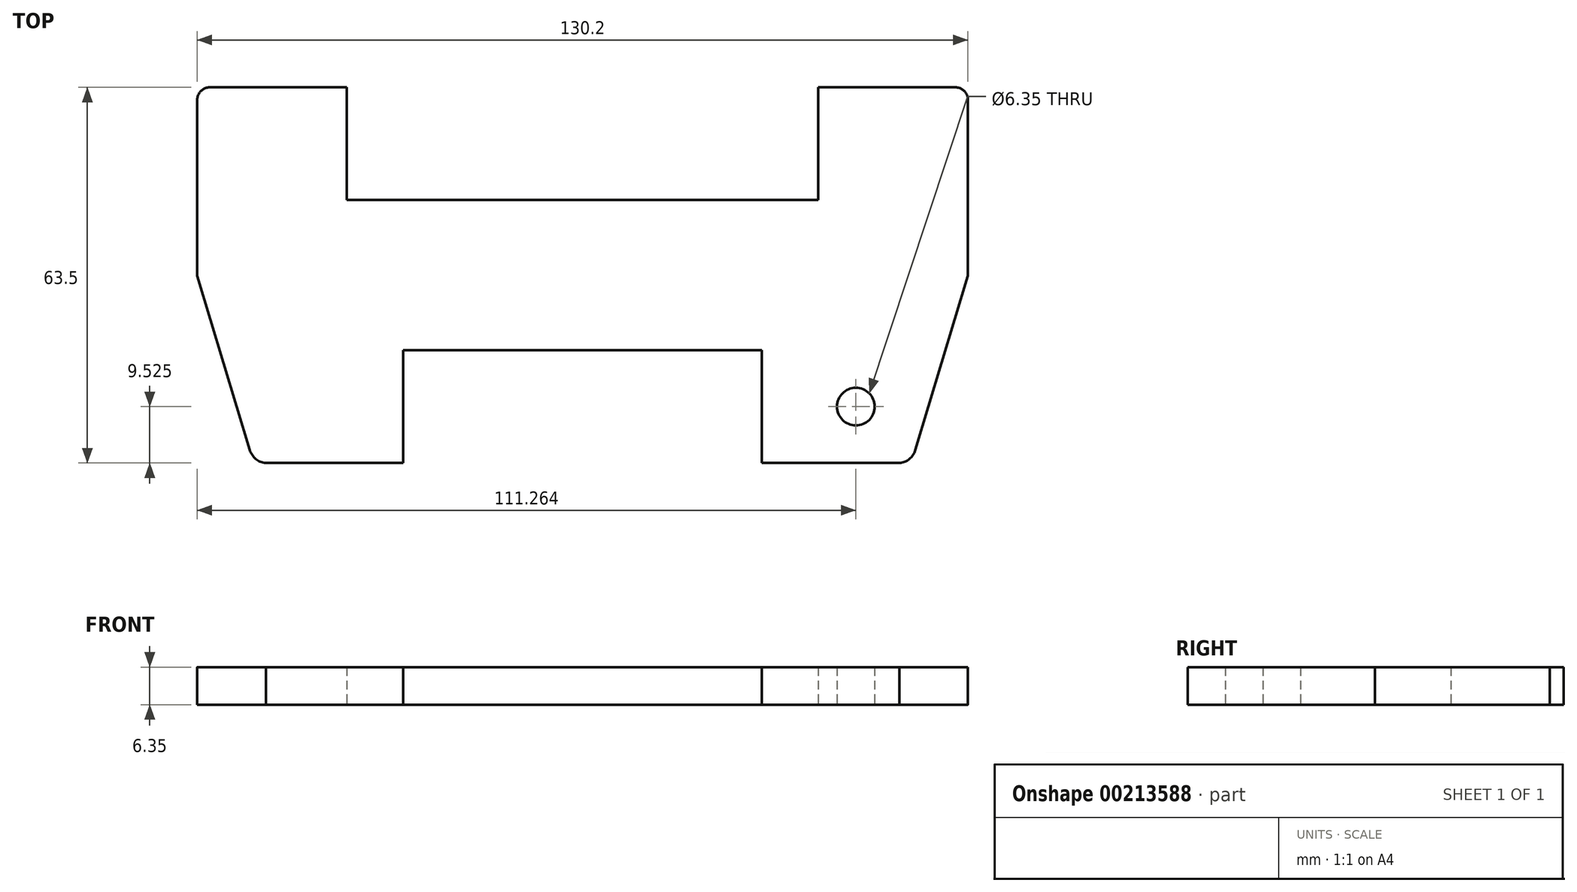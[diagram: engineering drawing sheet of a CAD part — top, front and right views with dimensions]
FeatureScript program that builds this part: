
annotation { "Feature Type Name" : "Feature", "Feature Type Description" : "" }
export const myFeature = defineFeature(function(context is Context, id is Id, definition is map)
    precondition{}
    {
        {
            var Q0;
            Q0=qCreatedBy(makeId("Top.planeOp"),FACE);
            var sketch = newSketch(context, id + "F0", { "sketchPlane" : qUnion([Q0])});
            skLineSegment(sketch, "E0", {"start": v(0, 12.7) * mm, "end": v(-39.81, 12.7) * mm});
            skLineSegment(sketch, "E1", {"start": v(-39.81, 12.7) * mm, "end": v(-39.81, 31.75) * mm});
            skLineSegment(sketch, "E2", {"start": v(-39.81, 31.75) * mm, "end": v(-62.97, 31.75) * mm});
            skArc(sketch, "E3", {"start": v(-62.97, 31.75) * mm, "mid": v(-64.55, 31.05) * mm, "end": v(-65.08, 29.4) * mm});
            skLineSegment(sketch, "E4", {"start": v(-65.08, 29.4) * mm, "end": v(-65.08, -0.1) * mm});
            skLineSegment(sketch, "E5", {"start": v(0, -12.7) * mm, "end": v(-30.29, -12.7) * mm});
            skLineSegment(sketch, "E6", {"start": v(-30.29, -12.7) * mm, "end": v(-30.29, -31.75) * mm});
            skLineSegment(sketch, "E7", {"start": v(-30.29, -31.75) * mm, "end": v(-53.52, -31.75) * mm});
            skLineSegment(sketch, "E8", {"start": v(-65.08, -0.1) * mm, "end": v(-56.2, -29.6) * mm});
            skArc(sketch, "E9", {"start": v(-56.2, -29.6) * mm, "mid": v(-55.19, -31.09) * mm, "end": v(-53.52, -31.75) * mm});
            skLineSegment(sketch, "E10.MirrorCS", {"start": v(0, -12.7) * mm, "end": v(30.29, -12.7) * mm});
            skLineSegment(sketch, "E11.MirrorCS", {"start": v(0, 12.7) * mm, "end": v(39.81, 12.7) * mm});
            skLineSegment(sketch, "E12.MirrorCS", {"start": v(30.29, -31.75) * mm, "end": v(53.52, -31.75) * mm});
            skArc(sketch, "E13.MirrorCS", {"start": v(62.97, 31.75) * mm, "mid": v(64.55, 31.05) * mm, "end": v(65.08, 29.4) * mm});
            skLineSegment(sketch, "E14.MirrorCS", {"start": v(65.08, -0.1) * mm, "end": v(56.2, -29.6) * mm});
            skLineSegment(sketch, "E15.MirrorCS", {"start": v(30.29, -12.7) * mm, "end": v(30.29, -31.75) * mm});
            skArc(sketch, "E16.MirrorCS", {"start": v(56.2, -29.6) * mm, "mid": v(55.19, -31.09) * mm, "end": v(53.52, -31.75) * mm});
            skLineSegment(sketch, "E17.MirrorCS", {"start": v(65.08, 29.4) * mm, "end": v(65.08, -0.1) * mm});
            skLineSegment(sketch, "E18.MirrorCS", {"start": v(39.81, 12.7) * mm, "end": v(39.81, 31.75) * mm});
            skLineSegment(sketch, "E19.MirrorCS", {"start": v(39.81, 31.75) * mm, "end": v(62.97, 31.75) * mm});
            skCircle(sketch, "E20", {"center": v(46.16, -22.23) * mm, "radius": 3.18 * mm});
            skSolve(sketch);
        }
        {
            var Q0;
            Q0=makeQuery(id+"F0.imprint","IMPRINT",FACE,{"disambiguationData":[TD([[makeQuery(id+"F0.imprint","IMPRINT",EDGE,{"derivedFrom":sQuery(id+"F0.wireOp",EDGE,"E0")}),1.0]])]});
            extrude(context, id + "F1", {"entities" : qUnion([Q0]), "depth" : 6.35 * mm});
        }
    });
